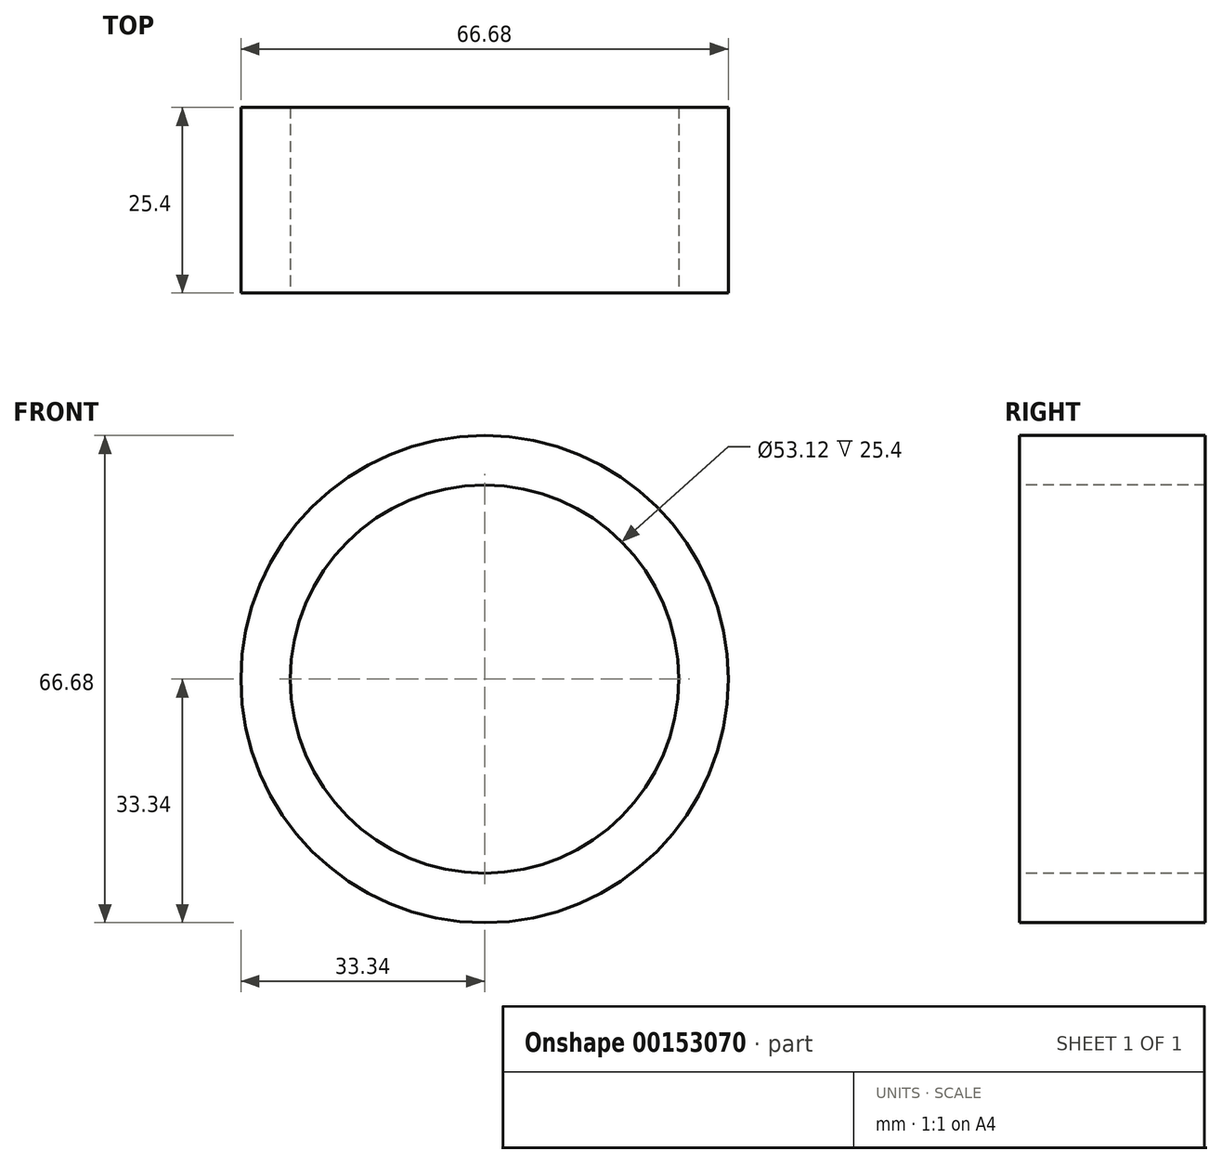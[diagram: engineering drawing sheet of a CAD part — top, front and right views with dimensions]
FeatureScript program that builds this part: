
annotation { "Feature Type Name" : "Feature", "Feature Type Description" : "" }
export const myFeature = defineFeature(function(context is Context, id is Id, definition is map)
    precondition{}
    {
        {
            var Q0;
            Q0=qCreatedBy(makeId("Front.planeOp"),FACE);
            var sketch = newSketch(context, id + "F0", { "sketchPlane" : qUnion([Q0])});
            skLineSegment(sketch, "E0.bottom", {"start": v(-87.99, 63.88) * mm, "end": v(87.99, 63.88) * mm});
            skLineSegment(sketch, "E0.top", {"start": v(-87.99, -63.88) * mm, "end": v(87.99, -63.88) * mm});
            skLineSegment(sketch, "E0.left", {"start": v(-87.99, 63.88) * mm, "end": v(-87.99, -63.88) * mm});
            skLineSegment(sketch, "E0.right", {"start": v(87.99, 63.88) * mm, "end": v(87.99, -63.88) * mm});
            skPoint(sketch, "E0.middle", {"position": v(0, 0) * mm});
            skSolve(sketch);
        }
        {
            var Q0;
            Q0 = qSketchRegion(id + "F0", true);
            extrude(context, id + "F1", {"entities" : qUnion([Q0]), "depth" : 25.4 * mm});
        }
        {
            var Q0;
            Q0=makeQuery(id+"F1.opExtrude","CAP_FACE",FACE,{"disambiguationData":[OSD([sQuery(id+"F0.wireOp",EDGE,"E0.bottom"),sQuery(id+"F0.wireOp",EDGE,"E0.top"),sQuery(id+"F0.wireOp",EDGE,"E0.left"),sQuery(id+"F0.wireOp",EDGE,"E0.right")])],"isStart":false});
            var sketch = newSketch(context, id + "F2", { "sketchPlane" : qUnion([Q0])});
            skCircle(sketch, "E1", {"center": v(0, 0) * mm, "radius": 33.34 * mm});
            skSolve(sketch);
        }
        {
            var Q0;
            Q0 = qSketchRegion(id + "F2", true);
            var Q1;
            Q1=sQuery(id+"F2.wireOp",EDGE,"E1");
            extrude(context, id + "F3", {"entities" : qUnion([Q0]), "operationType" : NewBodyOperationType.INTERSECT, "surfaceEntities" : qUnion([Q1]), "oppositeDirection" : true, "depth" : 25.4 * mm});
        }
        {
            var Q0;
            Q0=makeQuery(id+"F1.opExtrude","CAP_FACE",FACE,{"disambiguationData":[OSD([sQuery(id+"F0.wireOp",EDGE,"E0.bottom"),sQuery(id+"F0.wireOp",EDGE,"E0.top"),sQuery(id+"F0.wireOp",EDGE,"E0.left"),sQuery(id+"F0.wireOp",EDGE,"E0.right")])],"isStart":false});
            var sketch = newSketch(context, id + "F4", { "sketchPlane" : qUnion([Q0])});
            skCircle(sketch, "E2", {"center": v(0, 0) * mm, "radius": 26.56 * mm});
            skSolve(sketch);
        }
        {
            var Q0;
            Q0=makeQuery(id+"F4.imprint","IMPRINT",FACE,{"disambiguationData":[TD([[makeQuery(id+"F4.imprint","IMPRINT",EDGE,{"derivedFrom":sQuery(id+"F4.wireOp",EDGE,"E2")}),1.0]])]});
            extrude(context, id + "F5", {"entities" : qUnion([Q0]), "operationType" : NewBodyOperationType.REMOVE, "oppositeDirection" : true, "depth" : 25.4 * mm});
        }
    });
